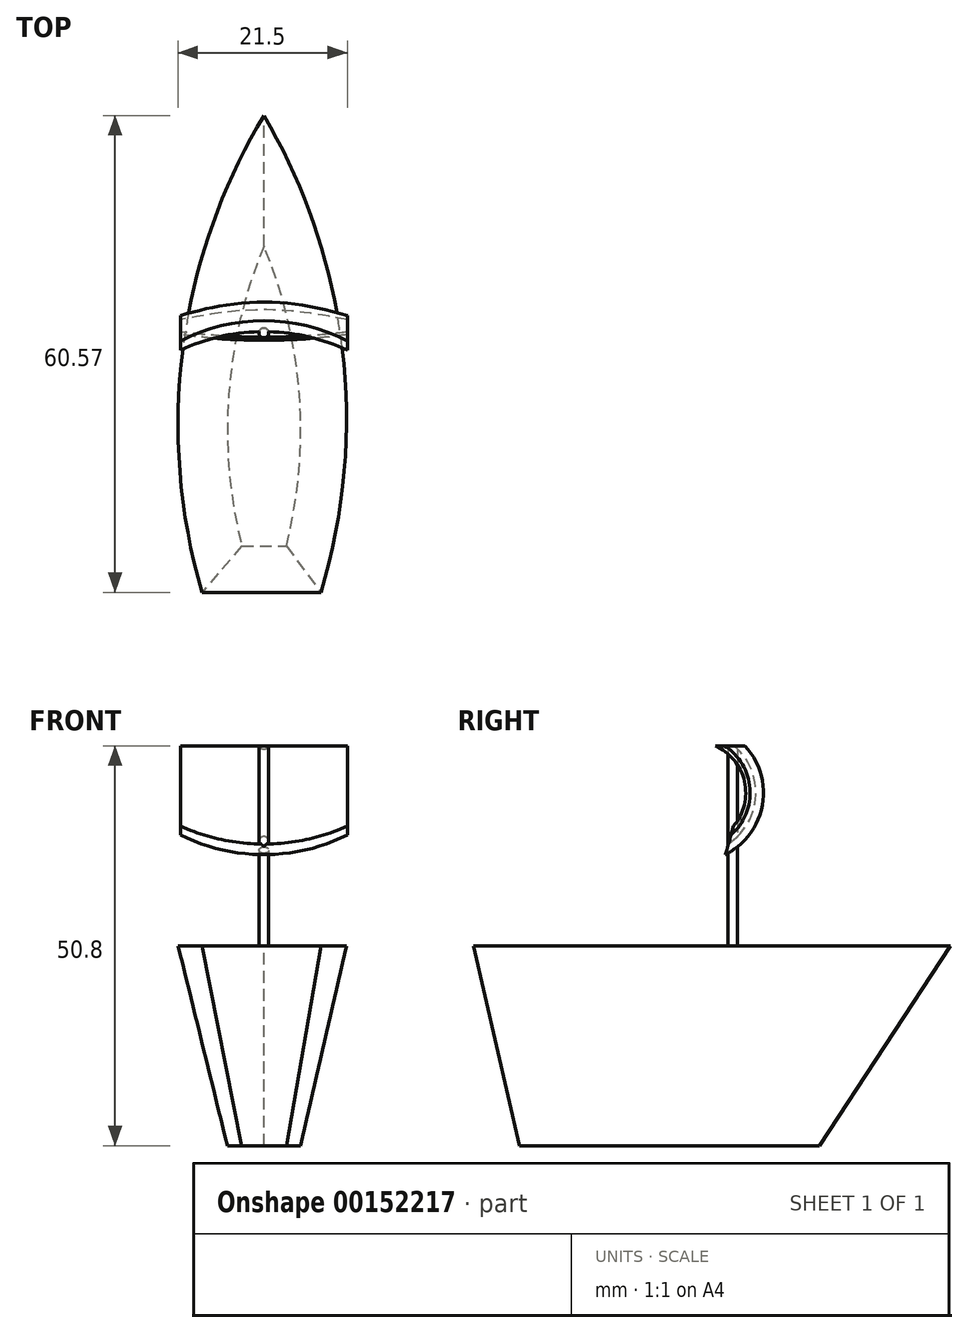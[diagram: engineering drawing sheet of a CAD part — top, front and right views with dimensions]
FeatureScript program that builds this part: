
annotation { "Feature Type Name" : "Feature", "Feature Type Description" : "" }
export const myFeature = defineFeature(function(context is Context, id is Id, definition is map)
    precondition{}
    {
        {
            var Q0;
            Q0=qCreatedBy(makeId("Top.planeOp"),FACE);
            var sketch = newSketch(context, id + "F0", { "sketchPlane" : qUnion([Q0])});
            skLineSegment(sketch, "E0", {"start": v(-2.8, -19.92) * mm, "end": v(2.85, -19.92) * mm});
            skArc(sketch, "E1", {"start": v(2.85, -19.92) * mm, "mid": v(4.5, -0.64) * mm, "end": v(0, 18.18) * mm});
            skArc(sketch, "E2", {"start": v(0, 18.18) * mm, "mid": v(-4.48, -0.64) * mm, "end": v(-2.8, -19.92) * mm});
            skSolve(sketch);
        }
        {
            var Q0;
            Q0=qCreatedBy(makeId("Top.planeOp"),FACE);
            cPlane(context, id + "F1", {"entities" : qUnion([Q0]), "cplaneType" : CPlaneType.OFFSET, "offset" : 25.4 * mm, "width" : 152.4 * mm, "height" : 152.4 * mm});
        }
        {
            var Q0;
            Q0=qCreatedBy(id+"F1.planeOp",FACE);
            var sketch = newSketch(context, id + "F2", { "sketchPlane" : qUnion([Q0])});
            skLineSegment(sketch, "E3", {"start": v(-7.87, -25.77) * mm, "end": v(7.25, -25.77) * mm});
            skArc(sketch, "E4", {"start": v(7.25, -25.77) * mm, "mid": v(9.94, 5.27) * mm, "end": v(0, 34.8) * mm});
            skArc(sketch, "E5", {"start": v(0, 34.8) * mm, "mid": v(-10.26, 5.34) * mm, "end": v(-7.87, -25.77) * mm});
            skSolve(sketch);
        }
        {
            var Q0;
            Q0=makeQuery(id+"F0.imprint","IMPRINT",FACE,{"disambiguationData":[TD([[makeQuery(id+"F0.imprint","IMPRINT",EDGE,{"derivedFrom":sQuery(id+"F0.wireOp",EDGE,"E0")}),1.0]])]});
            var Q1;
            Q1=makeQuery(id+"F2.imprint","IMPRINT",FACE,{"disambiguationData":[TD([[makeQuery(id+"F2.imprint","IMPRINT",EDGE,{"derivedFrom":sQuery(id+"F2.wireOp",EDGE,"E3")}),1.0]])]});
            loft(context, id + "F3", {"sheetProfilesArray" : [{ "sheetProfileEntities" : qUnion([Q0]) }, { "sheetProfileEntities" : qUnion([Q1]) }]});
        }
        {
            var Q0;
            Q0=makeQuery(id+"F3.opLoft","CAP_FACE",FACE,{"disambiguationData":[OSD([makeQuery(id+"F2.imprint","IMPRINT",FACE,{"disambiguationData":[TD([[makeQuery(id+"F2.imprint","IMPRINT",EDGE,{"derivedFrom":sQuery(id+"F2.wireOp",EDGE,"E3")}),1.0]])]})])],"isStart":true});
            var sketch = newSketch(context, id + "F4", { "sketchPlane" : qUnion([Q0])});
            skCircle(sketch, "E6", {"center": v(0, 7.18) * mm, "radius": 0.62 * mm});
            skSolve(sketch);
        }
        {
            var Q0;
            Q0=makeQuery(id+"F4.imprint","IMPRINT",FACE,{"disambiguationData":[TD([[makeQuery(id+"F4.imprint","IMPRINT",EDGE,{"derivedFrom":sQuery(id+"F4.wireOp",EDGE,"E6")}),1.0]])]});
            extrude(context, id + "F5", {"entities" : qUnion([Q0]), "operationType" : NewBodyOperationType.ADD, "depth" : 25.4 * mm});
        }
        {
            var Q0;
            Q0=qCreatedBy(id+"F1.planeOp",FACE);
            cPlane(context, id + "F6", {"entities" : qUnion([Q0]), "cplaneType" : CPlaneType.OFFSET, "offset" : 25.4 * mm, "width" : 152.4 * mm, "height" : 152.4 * mm});
        }
        {
            var Q0;
            Q0=qCreatedBy(id+"F6.planeOp",FACE);
            var sketch = newSketch(context, id + "F7", { "sketchPlane" : qUnion([Q0])});
            skArc(sketch, "E7", {"start": v(10.6, 4.97) * mm, "mid": v(0, 7.34) * mm, "end": v(-10.6, 4.97) * mm});
            skLineSegment(sketch, "E8", {"start": v(0, 7.34) * mm, "end": v(0, 0) * mm, "construction": true});
            skLineSegment(sketch, "E9", {"start": v(-10.6, 4.97) * mm, "end": v(10.6, 4.97) * mm, "construction": true});
            skLineSegment(sketch, "E10", {"start": v(-10.6, 4.97) * mm, "end": v(-10.6, 6.14) * mm});
            skLineSegment(sketch, "E11", {"start": v(10.6, 4.97) * mm, "end": v(10.6, 6.14) * mm});
            skArc(sketch, "E12", {"start": v(10.6, 6.14) * mm, "mid": v(0, 8.74) * mm, "end": v(-10.6, 6.14) * mm});
            skLineSegment(sketch, "E13", {"start": v(0, 7.34) * mm, "end": v(0, 8.74) * mm, "construction": true});
            skLineSegment(sketch, "E14", {"start": v(0, 8.74) * mm, "end": v(0, 8.04) * mm, "construction": true});
            skPoint(sketch, "E15", {"position": v(0, 8.74) * mm});
            skSolve(sketch);
        }
        {
            var Q0;
            Q0=qCreatedBy(makeId("Right.planeOp"),FACE);
            var sketch = newSketch(context, id + "F8", { "sketchPlane" : qUnion([Q0])});
            skArc(sketch, "E16", {"start": v(6.25, 36.98) * mm, "mid": v(10.94, 43.27) * mm, "end": v(8.74, 50.8) * mm});
            skPoint(sketch, "E17", {"position": v(6.25, 36.98) * mm});
            skSolve(sketch);
        }
        {
            var Q0;
            Q0=makeQuery(id+"F7.imprint","IMPRINT",FACE,{"disambiguationData":[TD([[makeQuery(id+"F7.imprint","IMPRINT",EDGE,{"derivedFrom":sQuery(id+"F7.wireOp",EDGE,"E7")}),-1.0]])]});
            var Q1;
            Q1=sQuery(id+"F8.wireOp",EDGE,"E16");
            sweep(context, id + "F9", {"operationType" : NewBodyOperationType.ADD, "profiles" : qUnion([Q0]), "path" : qUnion([Q1])});
        }
    });
